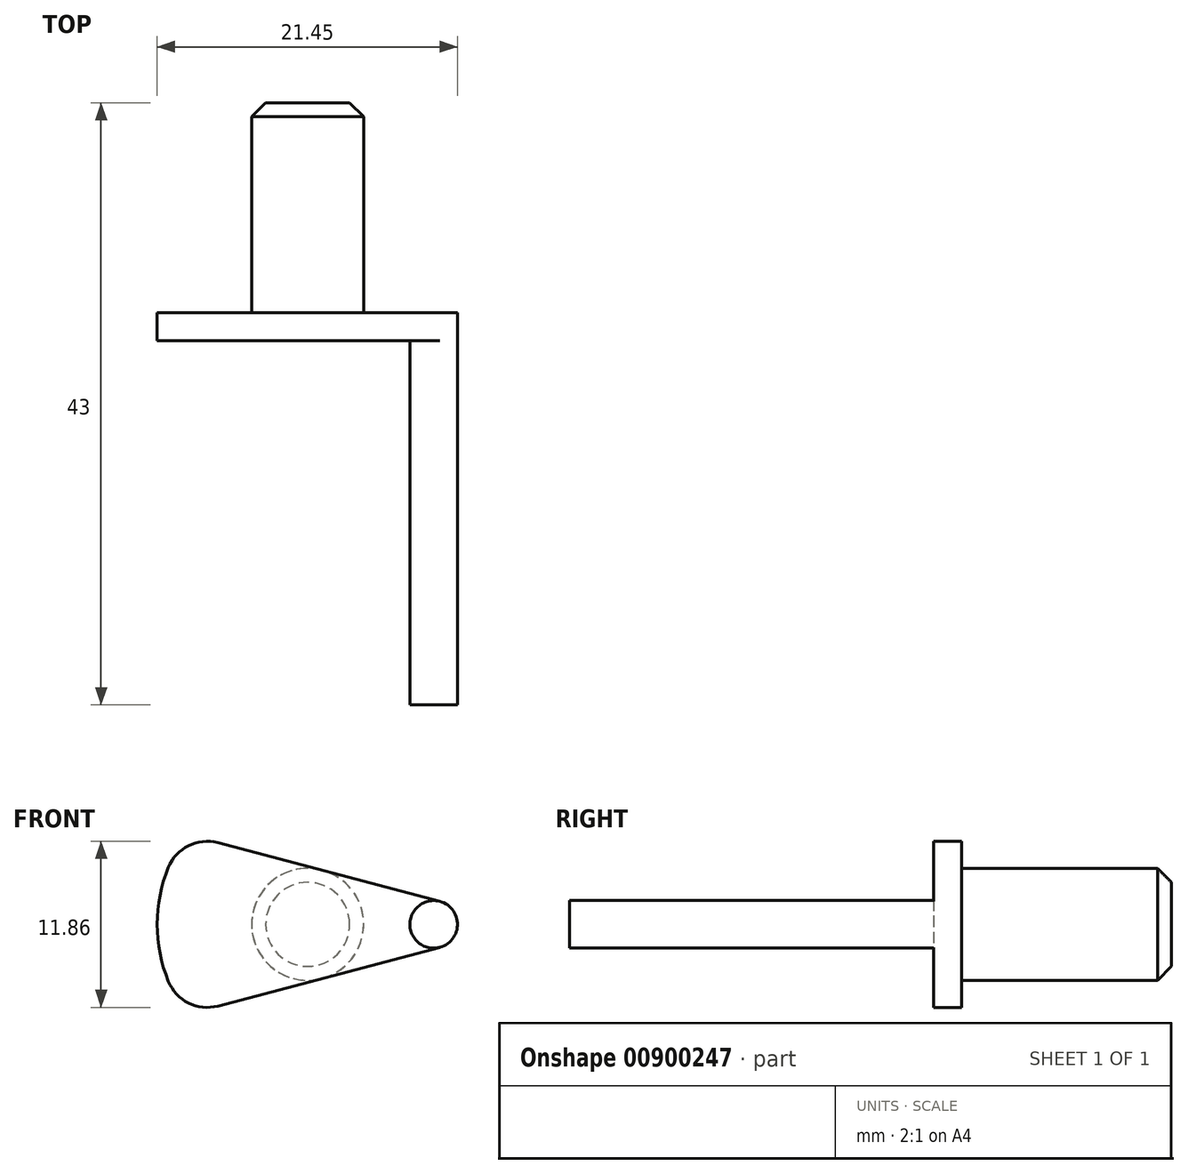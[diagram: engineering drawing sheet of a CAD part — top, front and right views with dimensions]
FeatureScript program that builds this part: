
annotation { "Feature Type Name" : "Feature", "Feature Type Description" : "" }
export const myFeature = defineFeature(function(context is Context, id is Id, definition is map)
    precondition{}
    {
        {
            var Q0;
            Q0=qCreatedBy(makeId("Front.planeOp"),FACE);
            var sketch = newSketch(context, id + "F0", { "sketchPlane" : qUnion([Q0])});
            skLineSegment(sketch, "E0", {"start": v(-10.85, 0) * mm, "end": v(10.7, 0) * mm, "construction": true});
            skArc(sketch, "E1", {"start": v(10.7, 0) * mm, "mid": v(10.35, 1.04) * mm, "end": v(9.43, 1.64) * mm});
            skArc(sketch, "E2", {"start": v(-9.95, 4.07) * mm, "mid": v(-10.55, 2.07) * mm, "end": v(-10.75, 0) * mm});
            skLineSegment(sketch, "E3", {"start": v(9.43, 1.64) * mm, "end": v(-6.4, 5.83) * mm});
            skPoint(sketch, "E4.visualSharp", {"position": v(-8.62, 6.42) * mm});
            skArc(sketch, "E4.filletArc", {"start": v(-6.4, 5.83) * mm, "mid": v(-8.51, 5.62) * mm, "end": v(-9.95, 4.07) * mm});
            skLineSegment(sketch, "E5.MirrorCS", {"start": v(9.43, -1.64) * mm, "end": v(-6.4, -5.83) * mm});
            skArc(sketch, "E6.MirrorCS", {"start": v(-6.4, -5.83) * mm, "mid": v(-8.51, -5.62) * mm, "end": v(-9.95, -4.07) * mm});
            skArc(sketch, "E7.MirrorCS", {"start": v(-9.95, -4.07) * mm, "mid": v(-10.55, -2.07) * mm, "end": v(-10.75, 0) * mm});
            skArc(sketch, "E8.MirrorCS", {"start": v(10.7, 0) * mm, "mid": v(10.35, -1.04) * mm, "end": v(9.43, -1.64) * mm});
            skPoint(sketch, "E9.orphan", {"position": v(10.85, 1.27) * mm});
            skPoint(sketch, "E10.orphan", {"position": v(10.85, -1.27) * mm});
            skCircle(sketch, "E11", {"center": v(0, 0) * mm, "radius": 4 * mm, "construction": true});
            skSolve(sketch);
        }
        {
            var Q0;
            Q0 = qSketchRegion(id + "F0", true);
            extrude(context, id + "F1", {"entities" : qUnion([Q0]), "depth" : 2 * mm, "offsetDistance" : 25 * mm});
        }
        {
            var Q0;
            Q0=makeQuery(id+"F1.opExtrude","CAP_FACE",FACE,{"disambiguationData":[OSD([sQuery(id+"F0.wireOp",EDGE,"E1"),sQuery(id+"F0.wireOp",EDGE,"E2"),sQuery(id+"F0.wireOp",EDGE,"E3"),sQuery(id+"F0.wireOp",EDGE,"E4.filletArc"),sQuery(id+"F0.wireOp",EDGE,"E5.MirrorCS"),sQuery(id+"F0.wireOp",EDGE,"E6.MirrorCS"),sQuery(id+"F0.wireOp",EDGE,"E7.MirrorCS"),sQuery(id+"F0.wireOp",EDGE,"E8.MirrorCS")])],"isStart":false});
            var sketch = newSketch(context, id + "F2", { "sketchPlane" : qUnion([Q0])});
            skCircle(sketch, "E12", {"center": v(9, 0) * mm, "radius": 1.7 * mm});
            skSolve(sketch);
        }
        {
            var Q0;
            {var subQ0=sQuery(id+"F2.wireOp",EDGE,"E12");Q0=makeQuery(id+"F2.imprint","IMPRINT",FACE,{"disambiguationData":[TD([[makeQuery(id+"F2.imprint","IMPRINT",EDGE,{"disambiguationData":[OD(0.0)],"derivedFrom":subQ0}),1.0]])]});}
            extrude(context, id + "F3", {"entities" : qUnion([Q0]), "operationType" : NewBodyOperationType.ADD, "depth" : 26 * mm, "offsetDistance" : 25 * mm});
        }
        {
            var Q0;
            Q0=makeQuery(id+"F1.opExtrude","CAP_FACE",FACE,{"disambiguationData":[OSD([sQuery(id+"F0.wireOp",EDGE,"E1"),sQuery(id+"F0.wireOp",EDGE,"E2"),sQuery(id+"F0.wireOp",EDGE,"E3"),sQuery(id+"F0.wireOp",EDGE,"E4.filletArc"),sQuery(id+"F0.wireOp",EDGE,"E5.MirrorCS"),sQuery(id+"F0.wireOp",EDGE,"E6.MirrorCS"),sQuery(id+"F0.wireOp",EDGE,"E7.MirrorCS"),sQuery(id+"F0.wireOp",EDGE,"E8.MirrorCS")])],"isStart":true});
            var sketch = newSketch(context, id + "F4", { "sketchPlane" : qUnion([Q0])});
            skCircle(sketch, "E13", {"center": v(0, 0) * mm, "radius": 4 * mm});
            skSolve(sketch);
        }
        {
            var Q0;
            Q0 = qSketchRegion(id + "F4", true);
            extrude(context, id + "F5", {"entities" : qUnion([Q0]), "operationType" : NewBodyOperationType.ADD, "depth" : 15 * mm, "offsetDistance" : 25 * mm});
        }
        {
            var Q0;
            Q0=makeQuery(id+"F5.opExtrude","CAP_EDGE",EDGE,{"disambiguationData":[OSD([sQuery(id+"F4.wireOp",EDGE,"E13")])],"isStart":false});
            chamfer(context, id + "F6", {"entities" : qUnion([Q0]), "width" : 1 * mm, "tangentPropagation" : true});
        }
    });
